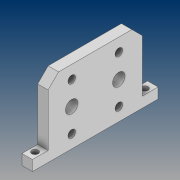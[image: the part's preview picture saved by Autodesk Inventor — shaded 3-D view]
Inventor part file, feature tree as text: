
AUTODESK INVENTOR PART (.ipt)
format: ipt  version: 2021 (Build 250183000, 183)  size: 155,648 bytes
history: native  units: mm
features: projected_geometry x5, sketch x4, extrude x2, hole x2, chamfer x1
ambient origin geometry x8: Origin, YZ Plane, XZ Plane, XY Plane, X Axis, Y Axis, Z Axis, Center Point
bodies: Solid1 (feature_tree)
feature tree (14):
  extrude  "Extrusion1"  Depth=120.0mm
  extrude  "Extrusion2"  Depth=52.0mm
  hole  "Hole1"  [1 undecoded]
  hole  "Hole2"  [1 undecoded]
  chamfer  "Chamfer1"  Distance=12.0mm
  sketch  "Sketch1"  dims[d0=35.0mm d1=120.0mm]
  sketch  "Sketch2"  dims[d2=45.0mm d3=52.0mm]
  projected_geometry  "Projected Loop1"
  projected_geometry  "Projected Loop2"
  sketch  "Sketch3"  dims[d4=36.0mm d5=75.0mm]
  projected_geometry  "Projected Loop3"
  sketch  "Sketch4"  dims[d6=15.0mm d7=9.0mm d8=12.0mm d9=12.0mm d10=10.0mm d11=0.0mm d14=60.0mm d15=0.0mm d16=45.0mm d17=7.2mm d18=6.0mm d19=4.0mm d20=2.0mm d21=90.0deg d22=8.0mm d23=20.594885mm d24=7.5mm d26=6.2mm d27=6.0mm d28=4.0mm d29=2.0mm d30=90.0deg d31=8.0mm d32=20.594885mm d33=10.0mm d34=2.0mm d35=45.0deg d36=15.0mm d37=15.0mm d38=7.5mm]
  projected_geometry  "Projected Loop4"
  projected_geometry  "Projected Loop5"
note: 2 required parameter values undecoded (feature->parameter linkage not recoverable at this tier; creation-order binding heuristic only, values carry confidence <= 0.55)
